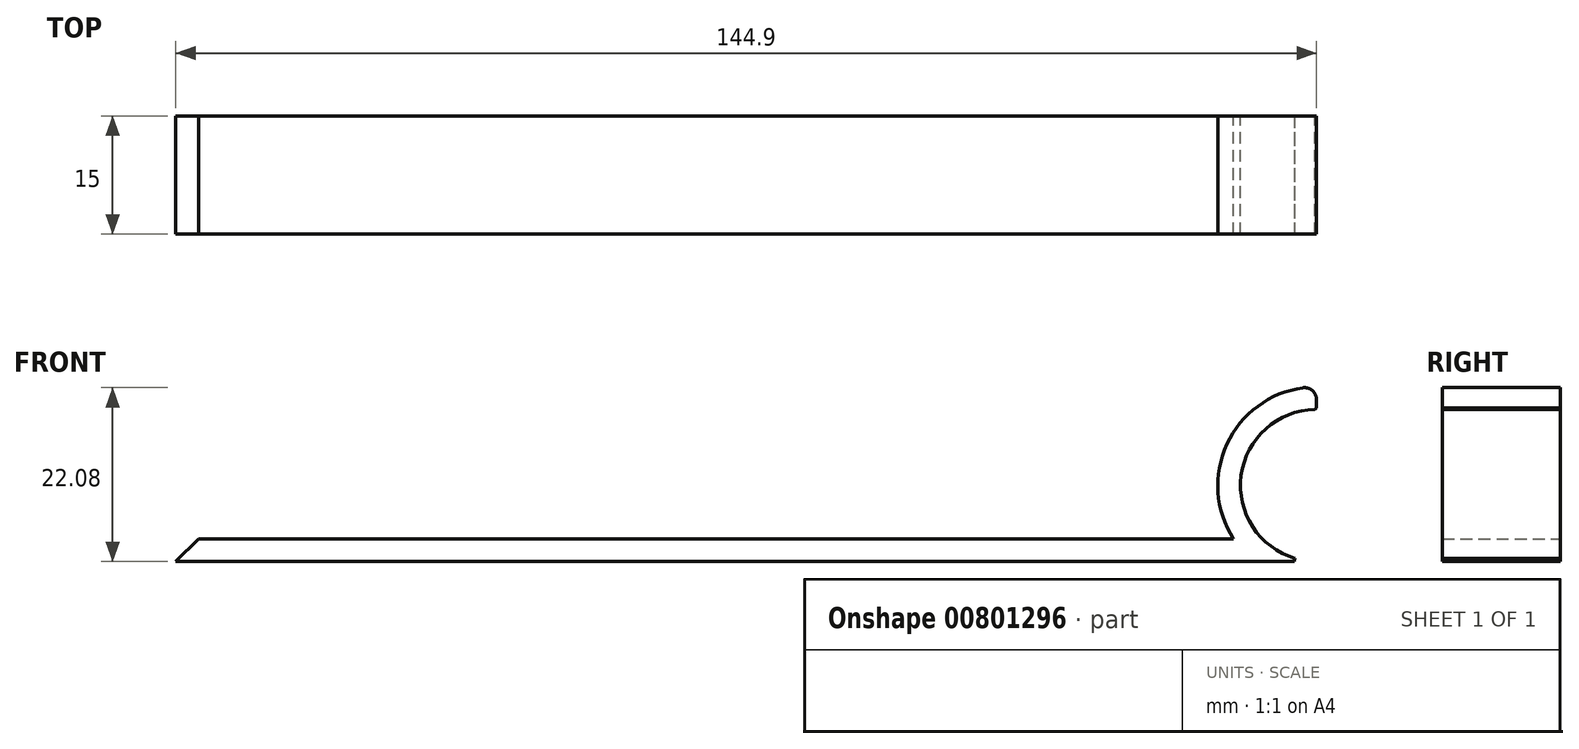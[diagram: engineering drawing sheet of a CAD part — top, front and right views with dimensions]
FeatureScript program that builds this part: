
annotation { "Feature Type Name" : "Feature", "Feature Type Description" : "" }
export const myFeature = defineFeature(function(context is Context, id is Id, definition is map)
    precondition{}
    {
        {
            var Q0;
            Q0=qCreatedBy(makeId("Front.planeOp"),FACE);
            var sketch = newSketch(context, id + "F0", { "sketchPlane" : qUnion([Q0])});
            skLineSegment(sketch, "E0.bottom", {"start": v(72.5, 1.44) * mm, "end": v(-72.5, 1.44) * mm});
            skLineSegment(sketch, "E0.top", {"start": v(72.5, -1.44) * mm, "end": v(-72.5, -1.44) * mm});
            skLineSegment(sketch, "E0.left", {"start": v(72.5, 1.44) * mm, "end": v(72.5, -1.44) * mm});
            skLineSegment(sketch, "E0.right", {"start": v(-72.5, 1.44) * mm, "end": v(-72.5, -1.44) * mm});
            skPoint(sketch, "E0.middle", {"position": v(0, 0) * mm});
            skLineSegment(sketch, "E1", {"start": v(72.5, -1.44) * mm, "end": v(72.5, 8.2) * mm, "construction": true});
            skCircle(sketch, "E2", {"center": v(72.5, 8.2) * mm, "radius": 9.65 * mm});
            skCircle(sketch, "E3", {"center": v(72.5, 8.2) * mm, "radius": 12.53 * mm});
            skLineSegment(sketch, "E4", {"start": v(72.5, 17.86) * mm, "end": v(72.5, 20.74) * mm});
            skSolve(sketch);
        }
        {
            var Q0;
            {var subQ0=sQuery(id+"F0.wireOp",EDGE,"E0.right");Q0=makeQuery(id+"F0.imprint","IMPRINT",FACE,{"disambiguationData":[TD([[makeQuery(id+"F0.imprint","IMPRINT",EDGE,{"derivedFrom":subQ0}),1.0]])]});}
            var Q1;
            {var subQ5=sQuery(id+"F0.wireOp",EDGE,"urySj7C3-RO8u-xJS9-4BbJ-Gt5VhAMPYNj5");Q1=makeQuery(id+"F0.imprint","IMPRINT",FACE,{"disambiguationData":[TD([[makeQuery(id+"F0.imprint","IMPRINT",EDGE,{"derivedFrom":subQ5}),1.0]])]});}
            var Q2;
            {var subQ5=sQuery(id+"F0.wireOp",EDGE,"E4");Q2=makeQuery(id+"F0.imprint","IMPRINT",FACE,{"disambiguationData":[TD([[makeQuery(id+"F0.imprint","IMPRINT",EDGE,{"derivedFrom":subQ5}),1.0]])]});}
            var Q3;
            {var subQ0=sQuery(id+"F0.wireOp",EDGE,"E3");var subQ1=sQuery(id+"F0.wireOp",EDGE,"E0.bottom");var subQ2=makeQuery(id+"F0.imprint","INTERSECT",VERTEX,{"derivedFrom":[subQ1,subQ0]});Q3=makeQuery(id+"F0.imprint","IMPRINT",FACE,{"disambiguationData":[TD([[makeQuery(id+"F0.imprint","IMPRINT",EDGE,{"disambiguationData":[TD([[subQ2,1.0]])],"derivedFrom":subQ1}),1.0]])]});}
            extrude(context, id + "F1", {"entities" : qUnion([Q0, Q1, Q2, Q3]), "depth" : 15 * mm, "offsetDistance" : 25 * mm});
        }
        {
            var Q0;
            Q0=makeQuery(id+"F1.opExtrude","SWEPT_EDGE",EDGE,{"disambiguationData":[OSD([sQuery(id+"F0.wireOp",EDGE,"E0.top"),sQuery(id+"F0.wireOp",EDGE,"E0.left"),sQuery(id+"F0.wireOp",EDGE,"E2")])]});
            var Q1;
            Q1=makeQuery(id+"F1.opExtrude","SWEPT_EDGE",EDGE,{"disambiguationData":[OSD([sQuery(id+"F0.wireOp",EDGE,"E2"),sQuery(id+"F0.wireOp",EDGE,"E4")])]});
            chamfer(context, id + "F2", {"entities" : qUnion([Q0, Q1]), "width" : 0.2 * mm, "tangentPropagation" : true});
        }
        {
            var Q0;
            Q0=makeQuery(id+"F1.opExtrude","SWEPT_EDGE",EDGE,{"disambiguationData":[OSD([sQuery(id+"F0.wireOp",EDGE,"E0.bottom"),sQuery(id+"F0.wireOp",EDGE,"E0.right")])]});
            chamfer(context, id + "F3", {"entities" : qUnion([Q0]), "chamferType" : ChamferType.OFFSET_ANGLE, "width" : 2.98 * mm, "oppositeDirection" : false, "angle" : 45 * degree, "tangentPropagation" : true});
        }
        {
            var Q0;
            Q0=makeQuery(id+"F1.opExtrude","SWEPT_EDGE",EDGE,{"disambiguationData":[OSD([sQuery(id+"F0.wireOp",EDGE,"E3"),sQuery(id+"F0.wireOp",EDGE,"E4")])]});
            fillet(context, id + "F4", {"entities" : qUnion([Q0]), "radius" : 1.5 * mm, "tangentPropagation" : true, "allowEdgeOverflow" : false});
        }
    });
